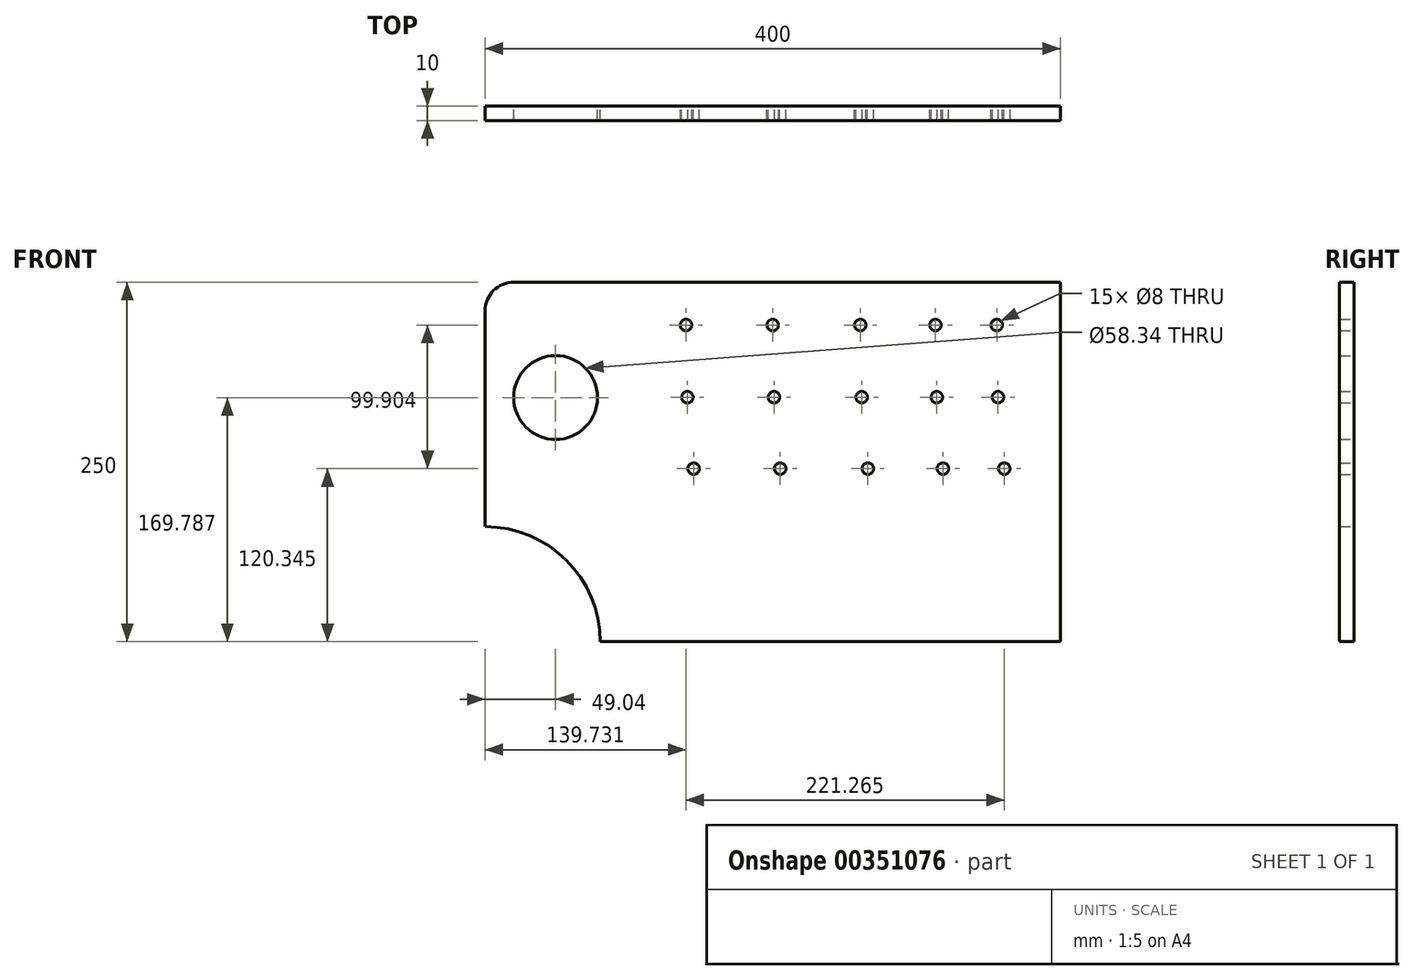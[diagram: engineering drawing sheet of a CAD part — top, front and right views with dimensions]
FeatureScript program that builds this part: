
annotation { "Feature Type Name" : "Feature", "Feature Type Description" : "" }
export const myFeature = defineFeature(function(context is Context, id is Id, definition is map)
    precondition{}
    {
        {
            var Q0;
            Q0=qCreatedBy(makeId("Front.planeOp"),FACE);
            var sketch = newSketch(context, id + "F0", { "sketchPlane" : qUnion([Q0])});
            skLineSegment(sketch, "E0.bottom", {"start": v(-180, 125) * mm, "end": v(200, 125) * mm});
            skLineSegment(sketch, "E0.top", {"start": v(-200, -125) * mm, "end": v(200, -125) * mm});
            skLineSegment(sketch, "E0.left", {"start": v(-200, 105) * mm, "end": v(-200, -125) * mm});
            skLineSegment(sketch, "E0.right", {"start": v(200, 125) * mm, "end": v(200, -125) * mm});
            skPoint(sketch, "E0.middle", {"position": v(0, 0) * mm});
            skLineSegment(sketch, "E1", {"start": v(-99.5, 95.25) * mm, "end": v(182.38, 95.25) * mm, "construction": true});
            skCircle(sketch, "E2", {"center": v(155.76, 95.25) * mm, "radius": 4 * mm});
            skPoint(sketch, "E3.visualSharp", {"position": v(-200, 125) * mm});
            skArc(sketch, "E3.filletArc", {"start": v(-180, 125) * mm, "mid": v(-194.14, 119.14) * mm, "end": v(-200, 105) * mm});
            skCircle(sketch, "E4", {"center": v(-150.96, 44.79) * mm, "radius": 29.17 * mm});
            skLineSegment(sketch, "E5", {"start": v(-98.47, 45.25) * mm, "end": v(183.41, 45.25) * mm, "construction": true});
            skLineSegment(sketch, "E6", {"start": v(-97.95, -4.75) * mm, "end": v(183.93, -4.75) * mm, "construction": true});
            skArc(sketch, "E7", {"start": v(-120, -125) * mm, "mid": v(-143.43, -68.43) * mm, "end": v(-200, -45) * mm});
            skCircle(sketch, "E8", {"center": v(113.14, 95.25) * mm, "radius": 4 * mm});
            skCircle(sketch, "E9", {"center": v(60.92, 95.25) * mm, "radius": 4 * mm});
            skCircle(sketch, "E10", {"center": v(0, 95.25) * mm, "radius": 4 * mm});
            skCircle(sketch, "E11", {"center": v(-60.27, 95.25) * mm, "radius": 4 * mm});
            skCircle(sketch, "E12", {"center": v(156.7, 45.04) * mm, "radius": 4 * mm});
            skCircle(sketch, "E13", {"center": v(114.07, 45.04) * mm, "radius": 4 * mm});
            skCircle(sketch, "E14", {"center": v(61.85, 45.04) * mm, "radius": 4 * mm});
            skCircle(sketch, "E15", {"center": v(0.93, 45.04) * mm, "radius": 4 * mm});
            skCircle(sketch, "E16", {"center": v(-59.34, 45.04) * mm, "radius": 4 * mm});
            skLineSegment(sketch, "E17", {"start": v(-94.27, -4.65) * mm, "end": v(187.61, -4.65) * mm, "construction": true});
            skCircle(sketch, "E18", {"center": v(161, -4.65) * mm, "radius": 4 * mm});
            skCircle(sketch, "E19", {"center": v(118.37, -4.65) * mm, "radius": 4 * mm});
            skCircle(sketch, "E20", {"center": v(66.16, -4.65) * mm, "radius": 4 * mm});
            skCircle(sketch, "E21", {"center": v(5.24, -4.65) * mm, "radius": 4 * mm});
            skCircle(sketch, "E22", {"center": v(-55.03, -4.65) * mm, "radius": 4 * mm});
            skSolve(sketch);
        }
        {
            var Q0;
            Q0=makeQuery(id+"F0.imprint","IMPRINT",FACE,{"disambiguationData":[TD([[makeQuery(id+"F0.imprint","IMPRINT",EDGE,{"derivedFrom":sQuery(id+"F0.wireOp",EDGE,"E0.bottom")}),-1.0]])]});
            extrude(context, id + "F1", {"entities" : qUnion([Q0]), "depth" : 10 * mm});
        }
    });
